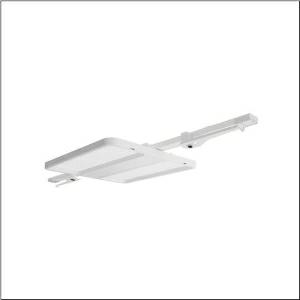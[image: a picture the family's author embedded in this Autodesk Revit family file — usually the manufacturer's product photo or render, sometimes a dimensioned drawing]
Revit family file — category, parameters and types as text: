
# Revit family: highbay_11_fur_modario_r__tragschiene_midi_51hn11da6fma_4b97
name_source: partatom
category: Lighting Fixtures
units: mm (PartAtom-declared; Revit-internal decimal feet)

## family parameters
Cut with Voids When Loaded = No
Host = Face
Light Source = No
Part Type = Normal
Room Calculation Point = No
Round Connector Dimension = Use Diameter
Shared = No

## types (1)
- --- (1 x LED, 14220 lm, 73.2 W, 6500K)
    Apparent Load = 73 VA
    CIE Flux Codes = 85 97 100 100 100
    Color Rendering = 80
    Color Temperature = 6500K
    Default Elevation = 1800 mm
    Description = high bay luminaire Highbay 11 for Modario® trunking rail midi; direct symmetric narrow distribution, light control with lens of PMMA; UGR ≤ 22 (X = 4H | Y = 8H | S = 0.25H | reflection values 70/50/20); luminous flux: 14.220lm; light colour: 865, colour temperature: 6500K, MacAdam ≤ 2 SDCM (initial), colour rendering: CRI > 80; luminous efficacy: 194,3lm/W; rated service life: 100.000h (L95/B50) at AT= 25°C; control: DALI 2; luminaire connection: plug, 5-pole, with phase selectionmains connection: 230..240V, AC 50/60Hz; connected load: 73,2W; protection rating (complete): IP64; insulation class (complete): insulation class I (protective earthing); protection symbol: D; impact resistance: IK07; certification: CE, ENEC, VDE, UKCA; internal wiring halogen-free; luminaire corresponds to IFS (International Featured Standards) requirements for safety and quality in the food industry; LABS conformity tested according to VDMA 24364:2018-05; housing frame of high-performance plastic PA6, matt traffic white (RAL 9016); cover of PMMA; fixing on rail side of steel, galvanised, white; blank cover of PC, traffic white (RAL 9016); dimension (LxWxH): 1.195 x 442 x 72mm; permissible operating ambient temperature: -40..+55°C (reducing of maximum allowable ambient temperature of 5°C with ceiling mounting); packaging unit: 1 piece
    Height = 72 mm  [stored 0.23622 ft]
    Lamp = 1 x LED
    Lamp Light Flux = 14220 lm
    Lamp Power = 73.2 W
    Lamp count = 1
    Length = 474 mm
    Luminous efficacy = 194 lm/W
    Manufacturer = Siteco
    ModVariant = No
    Model = 51HN11DA6FMA
    Mounting Place = Ceiling
    Mounting Type = Pendant
    Number of Poles = 1
    OnlyDefault = Yes
    Power Factor = 1
    Product Name = Highbay 11 für Modario® Tragschiene midi
    Product group = high bay luminaire
    ProductGroupID = 901
    Protection Class = Protection class I
    Protection Degree = IP 64
    RLX_Detail_Level = 1
    RLX_Emergency_Light_Flux = 0 lm
    RLX_Emergency_Type = 0
    RLX_Emergency_Type_DB = No
    RlxData = <blob elided: 18105 chars, md5=226d4d6c>
    Socket = socket
    Standby Power = 0 W
    System Light Flux = 14220 lm
    System Power = 73 W
    Type Comments = factory setting: luminous flux: 100 % | dim-lin: 254 | 339 mA
    Type Image = l_1363266.jpg
    URL = http://relux.com
    VarID = @adj_005933
    Voltage = 0 V
    Weight = 0.00 kg
    Width = 442 mm

note: [stored X ft] marks values corroborated as IEEE doubles in the binary element streams (Revit-internal decimal feet)

## geometry (parser evidence)
native form markers: Blend x4, Sweep x10
no freeform markers — native parametric forms only
